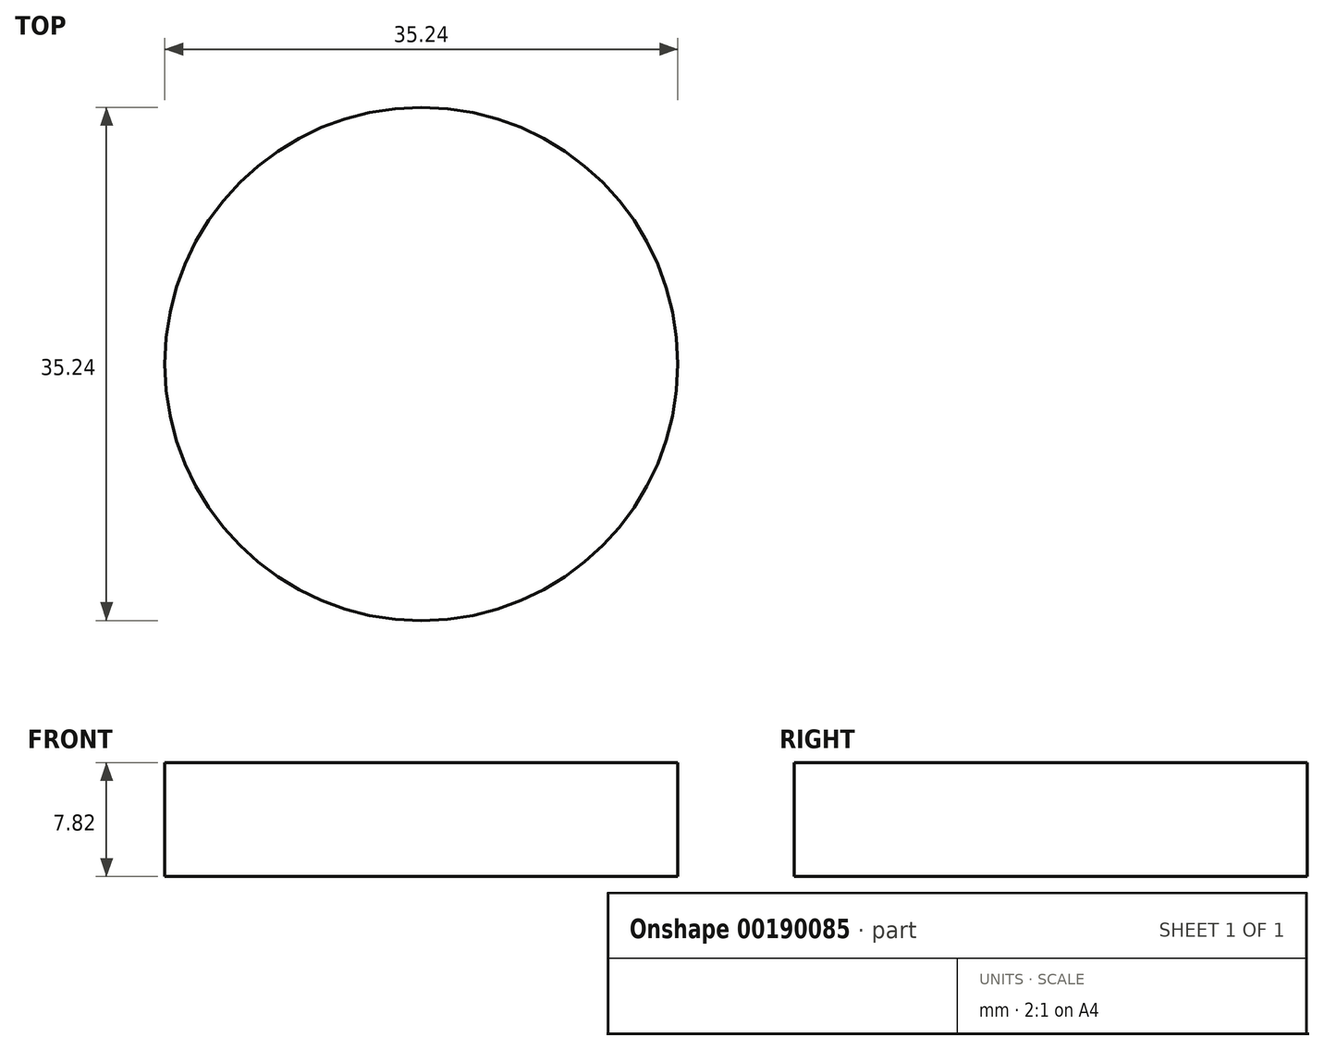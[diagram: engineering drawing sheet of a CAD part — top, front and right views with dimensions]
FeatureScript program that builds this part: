
annotation { "Feature Type Name" : "Feature", "Feature Type Description" : "" }
export const myFeature = defineFeature(function(context is Context, id is Id, definition is map)
    precondition{}
    {
        {
            var Q0;
            Q0=qCreatedBy(makeId("Front.planeOp"),FACE);
            var sketch = newSketch(context, id + "F0", { "sketchPlane" : qUnion([Q0])});
            skLineSegment(sketch, "E0.bottom", {"start": v(0, 0) * mm, "end": v(-17.62, 0) * mm});
            skLineSegment(sketch, "E0.top", {"start": v(0, 7.82) * mm, "end": v(-17.62, 7.82) * mm});
            skLineSegment(sketch, "E0.left", {"start": v(0, 0) * mm, "end": v(0, 7.82) * mm});
            skLineSegment(sketch, "E0.right", {"start": v(-17.62, 0) * mm, "end": v(-17.62, 7.82) * mm});
            skSolve(sketch);
        }
        {
            var Q0;
            Q0=makeQuery(id+"F0.imprint","IMPRINT",FACE,{"disambiguationData":[TD([[makeQuery(id+"F0.imprint","IMPRINT",EDGE,{"derivedFrom":sQuery(id+"F0.wireOp",EDGE,"E0.bottom")}),-1.0]])]});
            var Q1;
            Q1=sQuery(id+"F0.wireOp",EDGE,"E0.left");
            revolve(context, id + "F1", {"entities" : qUnion([Q0]), "axis" : qUnion([Q1]), "revolveType" : RevolveType.FULL});
        }
    });
